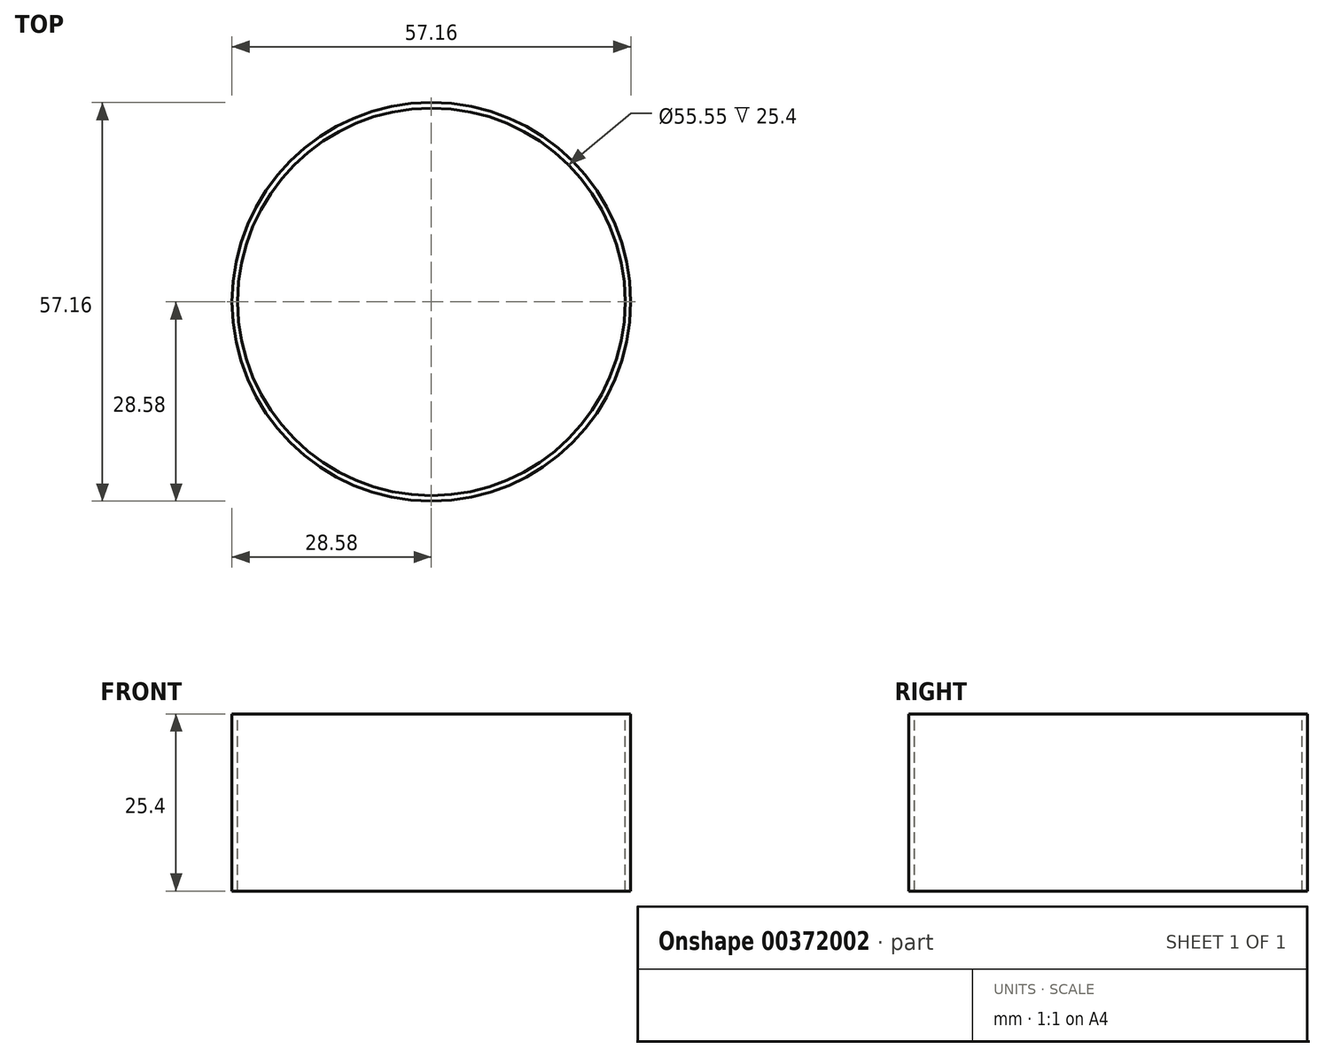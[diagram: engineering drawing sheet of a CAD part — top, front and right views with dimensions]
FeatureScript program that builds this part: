
annotation { "Feature Type Name" : "Feature", "Feature Type Description" : "" }
export const myFeature = defineFeature(function(context is Context, id is Id, definition is map)
    precondition{}
    {
        {
            var Q0;
            Q0=qCreatedBy(makeId("Front.planeOp"),FACE);
            var sketch = newSketch(context, id + "F0", { "sketchPlane" : qUnion([Q0])});
            skLineSegment(sketch, "E0.bottom", {"start": v(0, 0) * mm, "end": v(-28.57, 0) * mm});
            skLineSegment(sketch, "E0.top", {"start": v(0, 25.4) * mm, "end": v(-28.58, 25.4) * mm});
            skLineSegment(sketch, "E0.left", {"start": v(0, 0) * mm, "end": v(0, 25.4) * mm});
            skLineSegment(sketch, "E0.right", {"start": v(-28.57, 0) * mm, "end": v(-28.57, 25.4) * mm});
            skSolve(sketch);
        }
        {
            var Q0;
            Q0=makeQuery(id+"F0.imprint","IMPRINT",FACE,{"disambiguationData":[TD([[makeQuery(id+"F0.imprint","IMPRINT",EDGE,{"derivedFrom":sQuery(id+"F0.wireOp",EDGE,"E0.bottom")}),-1.0]])]});
            var Q1;
            Q1=sQuery(id+"F0.wireOp",EDGE,"E0.left");
            revolve(context, id + "F1", {"entities" : qUnion([Q0]), "axis" : qUnion([Q1]), "revolveType" : RevolveType.FULL});
        }
        {
            var Q0;
            Q0=makeQuery(id+"F1.opRevolve","SWEPT_FACE",FACE,{"disambiguationData":[OSD([sQuery(id+"F0.wireOp",EDGE,"E0.top")])]});
            var sketch = newSketch(context, id + "F2", { "sketchPlane" : qUnion([Q0])});
            skCircle(sketch, "E1", {"center": v(0, 0) * mm, "radius": 27.83 * mm});
            skSolve(sketch);
        }
        {
            var Q0;
            Q0=sQuery(id+"F2.wireOp",VERTEX,"E1.center");
            var Q1;
            Q1=makeQuery(id+"F1.opRevolve","SWEPT_BODY",BODY,{"disambiguationData":[OSD([sQuery(id+"F0.wireOp",EDGE,"E0.bottom"),sQuery(id+"F0.wireOp",EDGE,"E0.top"),sQuery(id+"F0.wireOp",EDGE,"E0.left"),sQuery(id+"F0.wireOp",EDGE,"E0.right")])]});
            hole(context, id + "F3", {"style" : HoleStyle.SIMPLE, "endStyle" : HoleEndStyle.THROUGH, "holeDiameter" : 55.55 * mm, "isTappedThrough" : true, "tappedDepth" : 12.7 * mm, "tapClearance" : 3, "locations" : qUnion([Q0]), "scope" : qUnion([Q1])});
        }
    });
